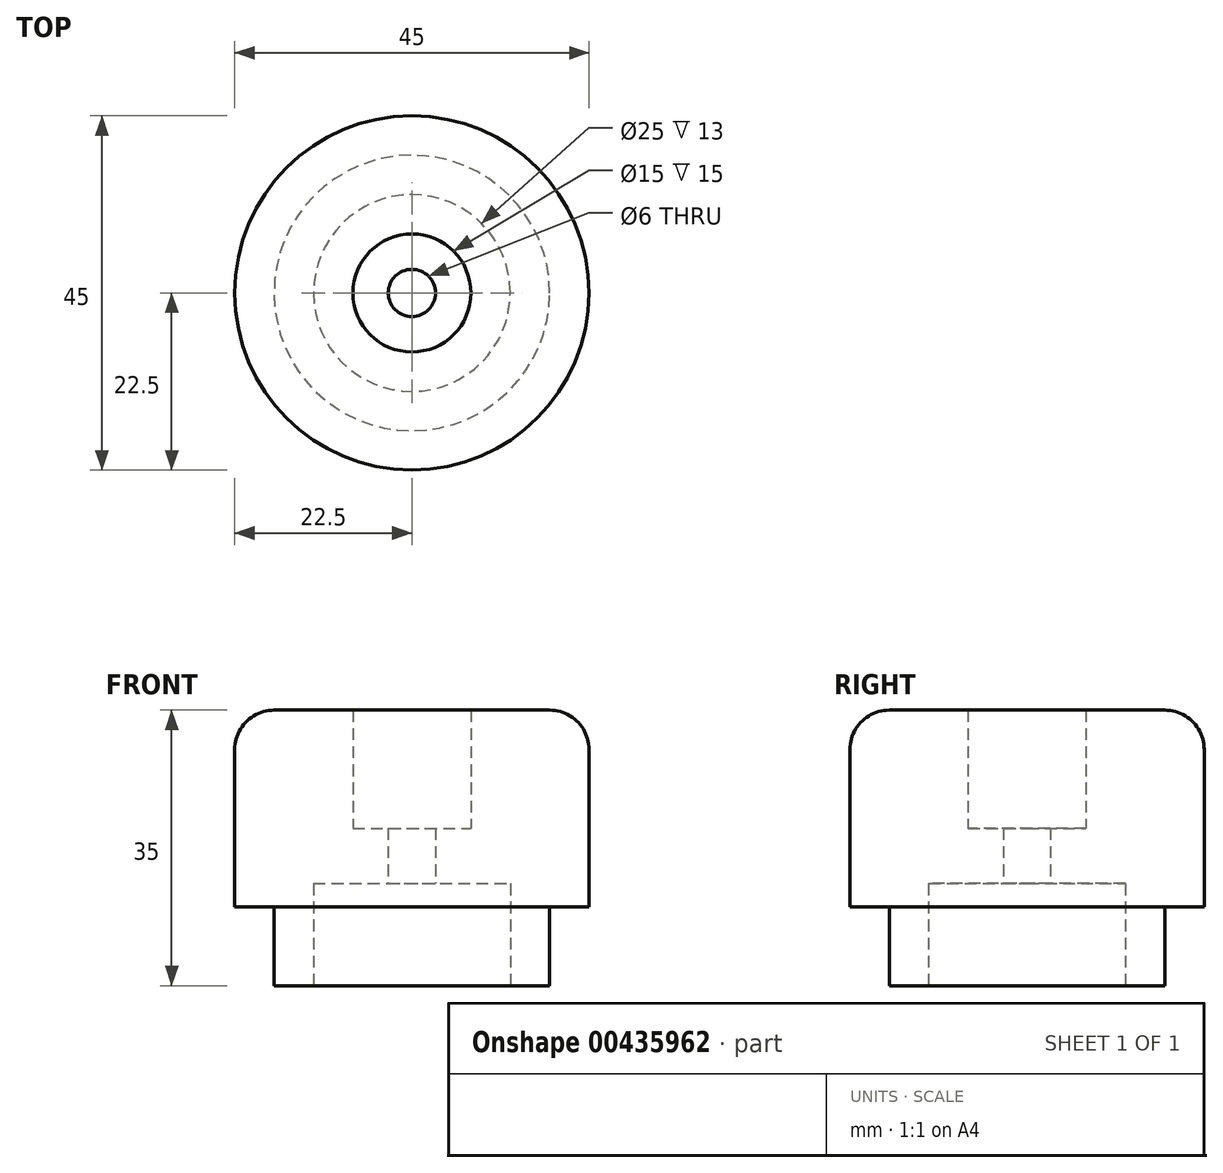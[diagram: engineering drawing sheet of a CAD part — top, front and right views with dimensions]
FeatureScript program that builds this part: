
annotation { "Feature Type Name" : "Feature", "Feature Type Description" : "" }
export const myFeature = defineFeature(function(context is Context, id is Id, definition is map)
    precondition{}
    {
        {
            var Q0;
            Q0=qCreatedBy(makeId("Front.planeOp"),FACE);
            var sketch = newSketch(context, id + "F0", { "sketchPlane" : qUnion([Q0])});
            skLineSegment(sketch, "E0.bottom", {"start": v(0, 0) * mm, "end": v(22.5, 0) * mm});
            skLineSegment(sketch, "E0.top", {"start": v(0, 35) * mm, "end": v(22.5, 35) * mm});
            skLineSegment(sketch, "E0.left", {"start": v(0, 0) * mm, "end": v(0, 35) * mm});
            skLineSegment(sketch, "E0.right", {"start": v(22.5, 0) * mm, "end": v(22.5, 35) * mm});
            skLineSegment(sketch, "E1", {"start": v(7.5, 35) * mm, "end": v(7.5, 0) * mm});
            skLineSegment(sketch, "E2", {"start": v(3, 35) * mm, "end": v(3, 0) * mm});
            skLineSegment(sketch, "E3", {"start": v(12.5, 35) * mm, "end": v(12.5, 0) * mm});
            skLineSegment(sketch, "E4", {"start": v(17.5, 35) * mm, "end": v(17.5, 0) * mm});
            skLineSegment(sketch, "E5", {"start": v(0, 10) * mm, "end": v(22.5, 10) * mm});
            skLineSegment(sketch, "E6", {"start": v(0, 13) * mm, "end": v(22.5, 13) * mm});
            skLineSegment(sketch, "E7", {"start": v(0, 20) * mm, "end": v(22.5, 20) * mm});
            skSolve(sketch);
        }
        {
            var Q0;
            {var subQ0=sQuery(id+"F0.wireOp",EDGE,"E7");var subQ1=sQuery(id+"F0.wireOp",EDGE,"E1");var subQ2=makeQuery(id+"F0.imprint","INTERSECT",VERTEX,{"derivedFrom":[subQ1,subQ0]});Q0=makeQuery(id+"F0.imprint","IMPRINT",FACE,{"disambiguationData":[TD([[makeQuery(id+"F0.imprint","IMPRINT",EDGE,{"disambiguationData":[TD([[subQ2,-1.0]])],"derivedFrom":subQ1}),-1.0]])]});}
            var Q1;
            {var subQ0=sQuery(id+"F0.wireOp",EDGE,"E5");var subQ1=sQuery(id+"F0.wireOp",EDGE,"E0.right");var subQ2=makeQuery(id+"F0.imprint","INTERSECT",VERTEX,{"derivedFrom":[subQ1,subQ0]});Q1=makeQuery(id+"F0.imprint","IMPRINT",FACE,{"disambiguationData":[TD([[makeQuery(id+"F0.imprint","IMPRINT",EDGE,{"disambiguationData":[TD([[subQ2,-1.0]])],"derivedFrom":subQ1}),1.0]])]});}
            var Q2;
            {var subQ0=sQuery(id+"F0.wireOp",EDGE,"E6");var subQ1=sQuery(id+"F0.wireOp",EDGE,"E0.right");var subQ2=makeQuery(id+"F0.imprint","INTERSECT",VERTEX,{"derivedFrom":[subQ1,subQ0]});Q2=makeQuery(id+"F0.imprint","IMPRINT",FACE,{"disambiguationData":[TD([[makeQuery(id+"F0.imprint","IMPRINT",EDGE,{"disambiguationData":[TD([[subQ2,-1.0]])],"derivedFrom":subQ1}),1.0]])]});}
            var Q3;
            {var subQ0=sQuery(id+"F0.wireOp",EDGE,"E0.right");var subQ1=sQuery(id+"F0.wireOp",EDGE,"E0.top");var subQ2=makeQuery(id+"F0.imprint","INTERSECT",VERTEX,{"derivedFrom":[subQ1,subQ0]});Q3=makeQuery(id+"F0.imprint","IMPRINT",FACE,{"disambiguationData":[TD([[makeQuery(id+"F0.imprint","IMPRINT",EDGE,{"disambiguationData":[TD([[subQ2,1.0]])],"derivedFrom":subQ1}),-1.0]])]});}
            var Q4;
            {var subQ0=sQuery(id+"F0.wireOp",EDGE,"E3");var subQ1=sQuery(id+"F0.wireOp",EDGE,"E0.top");var subQ2=makeQuery(id+"F0.imprint","INTERSECT",VERTEX,{"derivedFrom":[subQ1,subQ0]});Q4=makeQuery(id+"F0.imprint","IMPRINT",FACE,{"disambiguationData":[TD([[makeQuery(id+"F0.imprint","IMPRINT",EDGE,{"disambiguationData":[TD([[subQ2,-1.0]])],"derivedFrom":subQ1}),-1.0]])]});}
            var Q5;
            {var subQ0=sQuery(id+"F0.wireOp",EDGE,"E1");var subQ1=sQuery(id+"F0.wireOp",EDGE,"E0.top");var subQ2=makeQuery(id+"F0.imprint","INTERSECT",VERTEX,{"derivedFrom":[subQ1,subQ0]});Q5=makeQuery(id+"F0.imprint","IMPRINT",FACE,{"disambiguationData":[TD([[makeQuery(id+"F0.imprint","IMPRINT",EDGE,{"disambiguationData":[TD([[subQ2,-1.0]])],"derivedFrom":subQ1}),-1.0]])]});}
            var Q6;
            {var subQ0=sQuery(id+"F0.wireOp",EDGE,"E7");var subQ1=sQuery(id+"F0.wireOp",EDGE,"E1");var subQ2=makeQuery(id+"F0.imprint","INTERSECT",VERTEX,{"derivedFrom":[subQ1,subQ0]});Q6=makeQuery(id+"F0.imprint","IMPRINT",FACE,{"disambiguationData":[TD([[makeQuery(id+"F0.imprint","IMPRINT",EDGE,{"disambiguationData":[TD([[subQ2,-1.0]])],"derivedFrom":subQ1}),1.0]])]});}
            var Q7;
            {var subQ0=sQuery(id+"F0.wireOp",EDGE,"E7");var subQ1=sQuery(id+"F0.wireOp",EDGE,"E3");var subQ2=makeQuery(id+"F0.imprint","INTERSECT",VERTEX,{"derivedFrom":[subQ1,subQ0]});Q7=makeQuery(id+"F0.imprint","IMPRINT",FACE,{"disambiguationData":[TD([[makeQuery(id+"F0.imprint","IMPRINT",EDGE,{"disambiguationData":[TD([[subQ2,-1.0]])],"derivedFrom":subQ1}),1.0]])]});}
            var Q8;
            {var subQ0=sQuery(id+"F0.wireOp",EDGE,"E3");var subQ1=sQuery(id+"F0.wireOp",EDGE,"E0.bottom");var subQ2=makeQuery(id+"F0.imprint","INTERSECT",VERTEX,{"derivedFrom":[subQ1,subQ0]});Q8=makeQuery(id+"F0.imprint","IMPRINT",FACE,{"disambiguationData":[TD([[makeQuery(id+"F0.imprint","IMPRINT",EDGE,{"disambiguationData":[TD([[subQ2,-1.0]])],"derivedFrom":subQ1}),1.0]])]});}
            var Q9;
            {var subQ0=sQuery(id+"F0.wireOp",EDGE,"E6");var subQ1=sQuery(id+"F0.wireOp",EDGE,"E3");var subQ2=makeQuery(id+"F0.imprint","INTERSECT",VERTEX,{"derivedFrom":[subQ1,subQ0]});Q9=makeQuery(id+"F0.imprint","IMPRINT",FACE,{"disambiguationData":[TD([[makeQuery(id+"F0.imprint","IMPRINT",EDGE,{"disambiguationData":[TD([[subQ2,-1.0]])],"derivedFrom":subQ1}),1.0]])]});}
            var Q10;
            Q10=sQuery(id+"F0.wireOp",EDGE,"E0.left");
            revolve(context, id + "F1", {"entities" : qUnion([Q0, Q1, Q2, Q3, Q4, Q5, Q6, Q7, Q8, Q9]), "axis" : qUnion([Q10]), "revolveType" : RevolveType.FULL});
        }
        {
            var Q0;
            Q0=makeQuery(id+"F1.opRevolve","SWEPT_EDGE",EDGE,{"disambiguationData":[OSD([sQuery(id+"F0.wireOp",EDGE,"E0.top"),sQuery(id+"F0.wireOp",EDGE,"E0.right")])]});
            fillet(context, id + "F2", {"entities" : qUnion([Q0]), "radius" : 5 * mm, "tangentPropagation" : true, "allowEdgeOverflow" : false});
        }
    });
